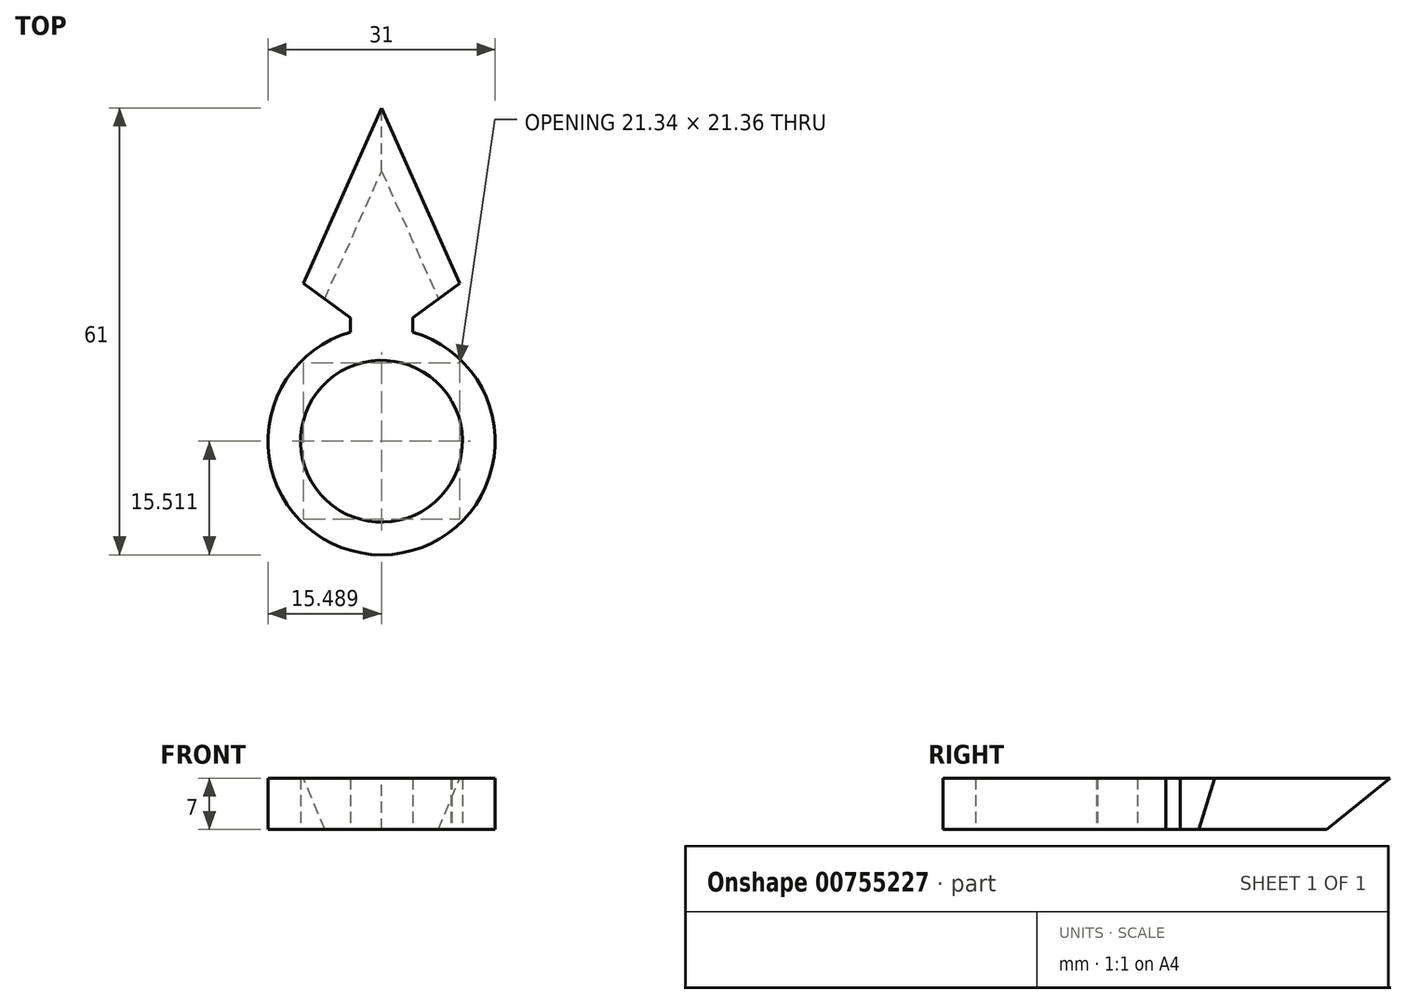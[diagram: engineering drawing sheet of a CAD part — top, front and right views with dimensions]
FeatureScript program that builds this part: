
annotation { "Feature Type Name" : "Feature", "Feature Type Description" : "" }
export const myFeature = defineFeature(function(context is Context, id is Id, definition is map)
    precondition{}
    {
        {
            var Q0;
            Q0=qCreatedBy(makeId("Top.planeOp"),FACE);
            var sketch = newSketch(context, id + "F0", { "sketchPlane" : qUnion([Q0])});
            skCircle(sketch, "E0", {"center": v(0, 0) * mm, "radius": 15.5 * mm});
            skCircle(sketch, "E1", {"center": v(0, 0) * mm, "radius": 11.05 * mm});
            skSolve(sketch);
        }
        {
            var Q0;
            Q0 = qSketchRegion(id + "F0", true);
            extrude(context, id + "F1", {"entities" : qUnion([Q0]), "depth" : 7 * mm, "offsetDistance" : 25.4 * mm});
        }
        {
            var Q0;
            Q0=qCreatedBy(makeId("Top.planeOp"),FACE);
            var sketch = newSketch(context, id + "F2", { "sketchPlane" : qUnion([Q0])});
            skLineSegment(sketch, "E2", {"start": v(0, 45.5) * mm, "end": v(10.65, 21.55) * mm});
            skLineSegment(sketch, "E3", {"start": v(10.65, 21.55) * mm, "end": v(4.27, 16.89) * mm});
            skLineSegment(sketch, "E4", {"start": v(4.27, 16.89) * mm, "end": v(4.27, 14.9) * mm});
            skArc(sketch, "E5.0", {"start": v(4.27, 14.9) * mm, "mid": v(0, 15.5) * mm, "end": v(-4.27, 14.9) * mm});
            skLineSegment(sketch, "E6", {"start": v(0, 45.5) * mm, "end": v(0, 15.5) * mm, "construction": true});
            skLineSegment(sketch, "E7.MirrorCS", {"start": v(-10.65, 21.55) * mm, "end": v(-4.27, 16.89) * mm});
            skLineSegment(sketch, "E8.MirrorCS", {"start": v(-4.27, 16.89) * mm, "end": v(-4.27, 14.9) * mm});
            skLineSegment(sketch, "E9.MirrorCS", {"start": v(0, 45.5) * mm, "end": v(-10.65, 21.55) * mm});
            skSolve(sketch);
        }
        {
            var Q0;
            Q0 = qSketchRegion(id + "F2", true);
            var Q1;
            Q1=makeQuery(id+"F1.opExtrude","CAP_FACE",FACE,{"disambiguationData":[OSD([sQuery(id+"F0.wireOp",EDGE,"E0"),sQuery(id+"F0.wireOp",EDGE,"E1")])],"isStart":false});
            extrude(context, id + "F3", {"entities" : qUnion([Q0]), "operationType" : NewBodyOperationType.ADD, "endBound" : BoundingType.UP_TO_SURFACE, "depth" : 25.4 * mm, "endBoundEntityFace" : qUnion([Q1]), "offsetDistance" : 25.4 * mm});
        }
        {
            var Q0;
            Q0=makeQuery(id+"F3.opExtrude","TWEAK_EDGE",EDGE,{"derivedFrom":[makeQuery(id+"F1.opExtrude","CAP_FACE",FACE,{"disambiguationData":[OSD([sQuery(id+"F0.wireOp",EDGE,"E0"),sQuery(id+"F0.wireOp",EDGE,"E1")])],"isStart":false}),makeQuery(id+"F2.imprint","IMPRINT",EDGE,{"derivedFrom":sQuery(id+"F2.wireOp",EDGE,"E9.MirrorCS")})]});
            var Q1;
            Q1=makeQuery(id+"F3.opExtrude","CAP_EDGE",EDGE,{"disambiguationData":[OSD([sQuery(id+"F2.wireOp",EDGE,"E9.MirrorCS")])],"isStart":true});
            var Q2;
            Q2=makeQuery(id+"F3.opExtrude","TWEAK_EDGE",EDGE,{"derivedFrom":[makeQuery(id+"F1.opExtrude","CAP_FACE",FACE,{"disambiguationData":[OSD([sQuery(id+"F0.wireOp",EDGE,"E0"),sQuery(id+"F0.wireOp",EDGE,"E1")])],"isStart":false}),makeQuery(id+"F2.imprint","IMPRINT",EDGE,{"derivedFrom":sQuery(id+"F2.wireOp",EDGE,"E2")})]});
            var Q3;
            Q3=makeQuery(id+"F3.opExtrude","CAP_EDGE",EDGE,{"disambiguationData":[OSD([sQuery(id+"F2.wireOp",EDGE,"E2")])],"isStart":true});
            chamfer(context, id + "F4", {"entities" : qUnion([Q0, Q1, Q2, Q3]), "chamferType" : ChamferType.TWO_OFFSETS, "width1" : 3.5 * mm, "oppositeDirection" : true, "width2" : 7 * mm, "tangentPropagation" : true});
        }
        {
            var Q0;
            Q0=qCreatedBy(makeId("Front.planeOp"),FACE);
            var sketch = newSketch(context, id + "F5", { "sketchPlane" : qUnion([Q0])});
            skLineSegment(sketch, "E10", {"start": v(0, 0) * mm, "end": v(0, 40.45) * mm, "construction": true});
            skSolve(sketch);
        }
        {
            var Q0;
            Q0=qCreatedBy(makeId("Top.planeOp"),FACE);
            var sketch = newSketch(context, id + "F6", { "sketchPlane" : qUnion([Q0])});
            skArc(sketch, "E11.0", {"start": v(9.61, 5.45) * mm, "mid": v(9.57, 5.53) * mm, "end": v(9.53, 5.6) * mm});
            skLineSegment(sketch, "E12", {"start": v(0, 0) * mm, "end": v(0, 8.2) * mm, "construction": true});
            skLineSegment(sketch, "E13", {"start": v(0, 0) * mm, "end": v(14.43, 8.33) * mm, "construction": true});
            skLineSegment(sketch, "E14", {"start": v(9.44, 5.45) * mm, "end": v(9.53, 5.6) * mm});
            skLineSegment(sketch, "E15.MirrorCS", {"start": v(9.44, 5.45) * mm, "end": v(9.61, 5.45) * mm});
            skSolve(sketch);
        }
        {
            var Q0;
            Q0 = qSketchRegion(id + "F6", true);
            var Q1;
            {var subQ0=sQuery(id+"F0.wireOp",EDGE,"E1");var subQ1=sQuery(id+"F0.wireOp",EDGE,"E0");Q1=makeQuery(id+"FL3O11X55JxvS0D_1.2.F3.boolean.opBoolean","MERGE",FACE,{"derivedFrom":[makeQuery(id+"FL3O11X55JxvS0D_1.1.F3.boolean.opBoolean","MERGE",FACE,{"derivedFrom":[makeQuery(id+"F3.boolean.opBoolean","MERGE",FACE,{"derivedFrom":[makeQuery(id+"F1.opExtrude","CAP_FACE",FACE,{"disambiguationData":[OSD([subQ1,subQ0])],"isStart":false}),makeQuery(id+"F3.opExtrude","CAP_FACE",FACE,{"disambiguationData":[OSD([subQ1,subQ0])],"isStart":false})]}),makeQuery(id+"FL3O11X55JxvS0D_1.1.F3.opExtrude","CAP_FACE",FACE,{"disambiguationData":[OSD([subQ1,subQ0])],"isStart":false})]}),makeQuery(id+"FL3O11X55JxvS0D_1.2.F3.opExtrude","CAP_FACE",FACE,{"disambiguationData":[OSD([subQ1,subQ0])],"isStart":false})]});}
            extrude(context, id + "F7", {"entities" : qUnion([Q0]), "operationType" : NewBodyOperationType.ADD, "endBound" : BoundingType.UP_TO_SURFACE, "depth" : 25 * mm, "endBoundEntityFace" : qUnion([Q1]), "offsetDistance" : 25 * mm});
        }
    });
